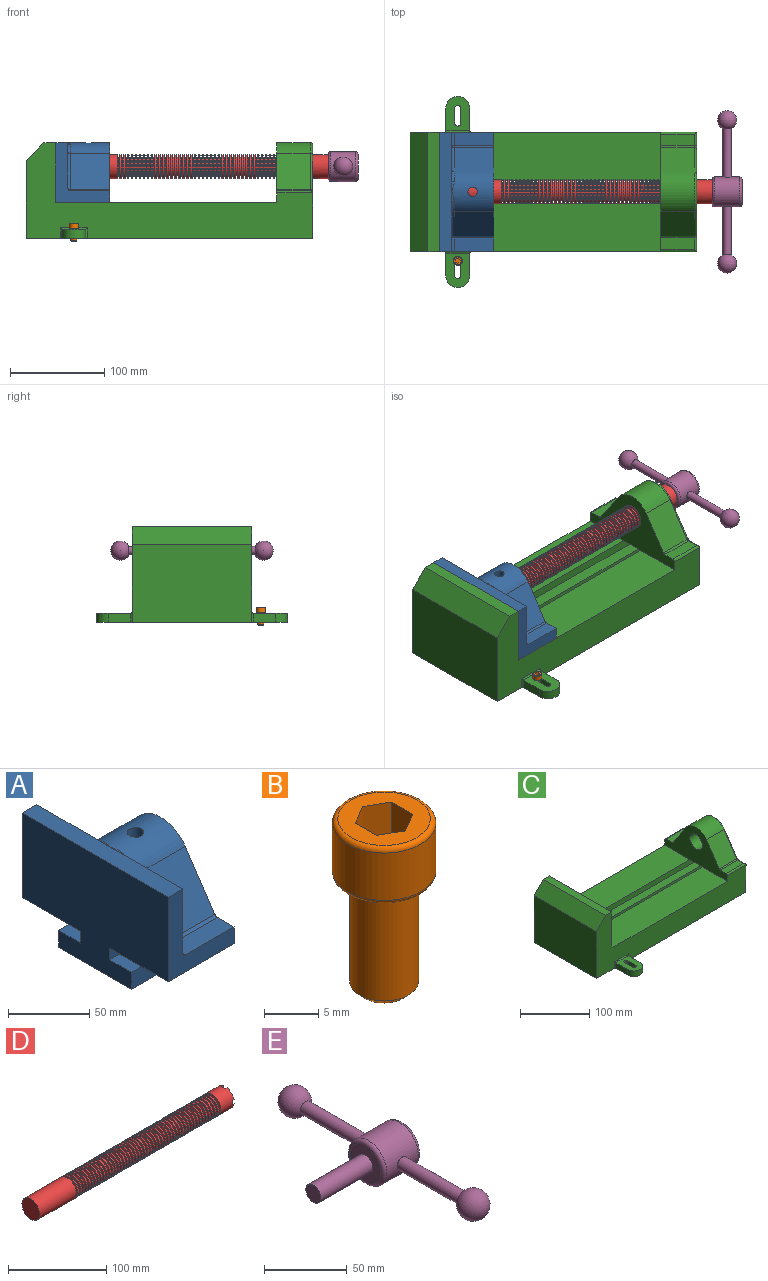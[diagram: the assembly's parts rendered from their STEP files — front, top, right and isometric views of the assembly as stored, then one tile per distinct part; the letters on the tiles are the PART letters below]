
ASSEMBLY  parts=5 mates=5
PART A: 36 faces, bbox 57.2x127x89 mm
  f0: plane 57.15x50.8mm, normal (0,0,-1), area 2903.2mm2, adj f6,f9,f10,f23
  f1: cylinder r=12.7mm len=44.45mm, axis (1,0,0), area 3464.3mm2, adj f6,f15,f16
  f2: plane 41.91x14.52mm, normal (0,0,1), area 608.5mm2, adj f6,f11,f24,f25
  f3: plane 51.86x48.26mm, normal (1,0,0), area 1495.7mm2, adj f8,f10,f31,f33,f35
  f4: plane 51.86x48.26mm, normal (1,0,0), area 1495.7mm2, adj f8,f11,f24,f28,f29
  f5: plane 57.15x50.8mm, normal (0,0,-1), area 2903.2mm2, adj f6,f9,f11,f22
  f6: plane 127x85.09mm, normal (1,0,0), area 5190.6mm2, adj f0,f1,f2,f5,f7,f10,f11,f12
  f7: plane 41.91x14.52mm, normal (0,0,1), area 608.5mm2, adj f6,f10,f30,f31
  f8: plane 127x12.7mm, normal (0,0,1), area 1612.9mm2, adj f3,f4,f9,f10,f11,f26,f34
  f9: plane 127x85.09mm, normal (-1,0,0), area 9096.8mm2, adj f0,f5,f8,f10,f11,f17,f18,f19
  f10: plane 63.5x57.15mm, normal (0,-1,0), area 1372.3mm2, adj f0,f3,f6,f7,f8,f9,f31
  f11: plane 63.5x57.15mm, normal (0,1,0), area 1372.3mm2, adj f2,f4,f5,f6,f8,f9,f24
  f12: plane 41.91x38.43mm, normal (0,-0.83,0.56), area 1939.2mm2, adj f6,f13,f30,f33
  f13: cylinder r=25.4mm len=44.45mm, axis (1,0,0), area 2026.5mm2, adj f6,f12,f14,f16,f26,f28,f34,f35
  f14: plane 41.91x38.43mm, normal (0,0.83,0.56), area 1939.2mm2, adj f6,f13,f25,f29
  f15: plane 25.4x25.4mm, normal (1,0,0), area 506.7mm2, adj f1
  f16: cylinder r=5.08mm len=13.76mm, axis (0,0,1), area 414mm2, adj f1,f13
  f17: plane 57.15x19.05mm, normal (0,0,1), area 1088.7mm2, adj f6,f9,f18,f23
  f18: plane 57.15x12.7mm, normal (0,-1,0), area 725.8mm2, adj f6,f9,f17,f19
  f19: plane 63.5x57.15mm, normal (0,0,-1), area 3629mm2, adj f6,f9,f18,f20
  f20: plane 57.15x12.7mm, normal (0,1,0), area 725.8mm2, adj f6,f9,f19,f21
  f21: plane 57.15x19.05mm, normal (0,0,1), area 1088.7mm2, adj f6,f9,f20,f22
  f22: plane 57.15x8.89mm, normal (0,1,0), area 508.1mm2, adj f5,f6,f9,f21
  f23: plane 57.15x8.89mm, normal (0,-1,0), area 508.1mm2, adj f0,f6,f9,f17
  f24: cylinder r=2.54mm len=14.52mm, axis (0,-1,0), area 57.9mm2, adj f2,f4,f11,f27
  f25: cylinder r=2.54mm len=41.91mm, axis (1,0,0), area 104.3mm2, adj f2,f6,f14,f27
  f26: bspline ~12.24x2.8mm, area 20.9mm2, adj f8,f13,f28
  f27: sphere r=2.54mm, area 6.3mm2, adj f24,f25,f29
  f28: torus R=27.94mm, axis (1,0,0), area 57.8mm2, adj f4,f13,f26,f29
  f29: cylinder r=2.54mm len=39.84mm, axis (0,-0.56,0.83), area 184.6mm2, adj f4,f14,f27,f28
  f30: cylinder r=2.54mm len=41.91mm, axis (1,0,0), area 104.3mm2, adj f6,f7,f12,f32
  f31: cylinder r=2.54mm len=14.52mm, axis (0,-1,0), area 57.9mm2, adj f3,f7,f10,f32
  f32: sphere r=2.54mm, area 6.3mm2, adj f30,f31,f33
  f33: cylinder r=2.54mm len=39.84mm, axis (0,-0.56,-0.83), area 184.6mm2, adj f3,f12,f32,f35
  f34: bspline ~12.24x2.8mm, area 20.9mm2, adj f8,f13,f35
  f35: torus R=27.94mm, axis (1,0,0), area 57.8mm2, adj f3,f13,f33,f34
PART B: 15 faces, bbox 10.3x10.3x19.1 mm
  f0: plane 8.51x8.51mm, normal (0,0,1), area 37.2mm2, adj f5,f6,f7,f8,f9,f10,f14
  f1: cylinder r=3.17mm len=11.94mm, axis (0,0,1), area 238.2mm2, adj f4,f12
  f2: plane 4.83x4.83mm, normal (0,0,-1), area 18.3mm2, adj f12
  f3: cylinder r=4.76mm len=9.53mm, axis (0,0,-1), area 159.6mm2, adj f13,f14
  f4: plane 8.51x8.51mm, normal (0,0,-1), area 25.2mm2, adj f1,f13
  f5: plane 4.83x2.38mm, normal (-0.5,-0.87,0), area 13.3mm2, adj f0,f6,f10,f11
  f6: plane 4.83x2.38mm, normal (0.5,-0.87,0), area 13.3mm2, adj f0,f5,f7,f11
  f7: plane 4.83x2.75mm, normal (1,0,0), area 13.3mm2, adj f0,f6,f8,f11
  f8: plane 4.83x2.38mm, normal (0.5,0.87,0), area 13.3mm2, adj f0,f7,f9,f11
  f9: plane 4.83x2.38mm, normal (-0.5,0.87,0), area 13.3mm2, adj f0,f8,f10,f11
  f10: plane 4.83x2.75mm, normal (-1,0,0), area 13.3mm2, adj f0,f5,f9,f11
  f11: plane 5.5x4.76mm, normal (0,0,1), area 19.6mm2, adj f5,f6,f7,f8,f9,f10
  f12: cone r=3.17mm half-angle=45deg, axis (0,0,1), area 18.9mm2, adj f1,f2
  f13: torus R=4.25mm, axis (0,0,1), area 23mm2, adj f3,f4
  f14: torus R=4.25mm, axis (0,0,1), area 23mm2, adj f0,f3
PART C: 61 faces, bbox 304.8x203.2x103.7 mm
  f0: plane 304.8x101.6mm, normal (0,1,0), area 13520.3mm2, adj f3,f4,f5,f6,f7,f8,f9,f16
  f1: plane 304.8x101.6mm, normal (0,-1,0), area 13520.3mm2, adj f2,f3,f5,f6,f7,f8,f9,f16
  f2: plane 234.95x50.8mm, normal (0,0,1), area 11935.5mm2, adj f1,f5,f16,f26
  f3: plane 127x99.06mm, normal (1,0,0), area 7097.5mm2, adj f0,f1,f9,f14,f17,f18,f19,f20
  f4: plane 234.95x50.8mm, normal (0,0,1), area 11935.5mm2, adj f0,f5,f16,f27
  f5: plane 127x101.6mm, normal (1,0,0), area 9516.1mm2, adj f0,f1,f2,f4,f6,f9,f18,f19
  f6: plane 127x12.7mm, normal (0,0,1), area 1612.9mm2, adj f0,f1,f5,f7
  f7: plane 127x19.05mm, normal (-0.71,0,0.71), area 3421.5mm2, adj f0,f1,f6,f8
  f8: plane 127x82.55mm, normal (-1,0,0), area 10483.8mm2, adj f0,f1,f7,f9
  f9: plane 304.8x203.2mm, normal (0,0,-1), area 33298.3mm2, adj f0,f1,f3,f5,f8,f21,f22,f39
  f10: plane 35.56x11.98mm, normal (0,0,1), area 426mm2, adj f16,f28,f29,f30
  f11: plane 38.43x35.56mm, normal (0,0.83,0.56), area 1645.4mm2, adj f12,f16,f29,f32
  f12: cylinder r=25.4mm len=42.19mm, axis (1,0,0), area 1770.2mm2, adj f11,f13,f16,f33
  f13: plane 38.43x35.56mm, normal (0,-0.83,0.56), area 1645.4mm2, adj f12,f16,f34,f35
  f14: cylinder r=12.7mm len=38.1mm, axis (1,0,0), area 3040.2mm2, adj f3,f16
  f15: plane 35.56x11.98mm, normal (0,0,1), area 426mm2, adj f16,f34,f36,f38
  f16: plane 127x63.5mm, normal (-1,0,0), area 4155.5mm2, adj f0,f1,f2,f4,f10,f11,f12,f13
  f17: plane 38.1x25.4mm, normal (0,0,-1), area 967.7mm2, adj f3,f16,f26,f27
  f18: plane 273.05x19.05mm, normal (0,0,-1), area 5201.6mm2, adj f3,f5,f19,f26
  f19: plane 273.05x12.7mm, normal (0,1,0), area 3467.7mm2, adj f3,f5,f18,f20
  f20: plane 273.05x19.05mm, normal (0,0,1), area 5201.6mm2, adj f3,f5,f19,f21
  f21: plane 273.05x16.51mm, normal (0,1,0), area 4508.1mm2, adj f3,f5,f9,f20
  f22: plane 273.05x16.51mm, normal (0,-1,0), area 4508.1mm2, adj f3,f5,f9,f23
  f23: plane 273.05x19.05mm, normal (0,0,1), area 5201.6mm2, adj f3,f5,f22,f24
  f24: plane 273.05x12.7mm, normal (0,-1,0), area 3467.7mm2, adj f3,f5,f23,f25
  f25: plane 273.05x19.05mm, normal (0,0,-1), area 5201.6mm2, adj f3,f5,f24,f27
  f26: plane 273.05x8.89mm, normal (0,1,0), area 2427.4mm2, adj f2,f3,f5,f17,f18
  f27: plane 273.05x8.89mm, normal (0,-1,0), area 2427.4mm2, adj f3,f4,f5,f17,f25
  f28: cylinder r=2.54mm len=38.1mm, axis (1,0,0), area 148.3mm2, adj f0,f10,f16,f30
  f29: cylinder r=2.54mm len=35.56mm, axis (-1,0,0), area 88.5mm2, adj f10,f11,f16,f31
  f30: cylinder r=2.54mm len=14.52mm, axis (0,1,0), area 54.3mm2, adj f3,f10,f28,f31
  f31: torus R=5.08mm, axis (-1,0,0), area 13.5mm2, adj f3,f29,f30,f32
  f32: cylinder r=2.54mm len=39.84mm, axis (0,0.56,-0.83), area 184.6mm2, adj f3,f11,f31,f33
  f33: torus R=22.86mm, axis (-1,0,0), area 191.4mm2, adj f3,f12,f32,f35
  f34: cylinder r=2.54mm len=35.56mm, axis (-1,0,0), area 88.5mm2, adj f13,f15,f16,f37
  f35: cylinder r=2.54mm len=39.84mm, axis (0,0.56,0.83), area 184.6mm2, adj f3,f13,f33,f37
  f36: cylinder r=2.54mm len=38.1mm, axis (-1,0,0), area 148.3mm2, adj f1,f15,f16,f38
  f37: torus R=5.08mm, axis (-1,0,0), area 13.5mm2, adj f3,f34,f35,f38
  f38: cylinder r=2.54mm len=14.52mm, axis (0,1,0), area 54.3mm2, adj f3,f15,f36,f37
  f39: plane 23.88x9.53mm, normal (-1,0,0), area 227.4mm2, adj f9,f45,f46,f60
  f40: plane 23.88x9.53mm, normal (1,0,0), area 227.4mm2, adj f9,f45,f46,f58
  f41: cylinder r=3.3mm len=9.53mm, axis (0,0,-1), area 98.8mm2, adj f9,f42,f44,f46
  f42: plane 15.62x9.53mm, normal (-1,0,0), area 148.8mm2, adj f9,f41,f43,f46
  f43: cylinder r=3.3mm len=9.53mm, axis (0,0,-1), area 98.8mm2, adj f9,f42,f44,f46
  f44: plane 15.62x9.53mm, normal (1,0,0), area 148.8mm2, adj f9,f41,f43,f46
  f45: cylinder r=12.7mm len=25.4mm, axis (0,0,-1), area 380mm2, adj f9,f39,f40,f46
  f46: plane 36.58x25.4mm, normal (0,0,1), area 722.4mm2, adj f39,f40,f41,f42,f43,f44,f45,f59
  f47: plane 23.88x9.53mm, normal (-1,0,0), area 227.4mm2, adj f9,f53,f54,f56
  f48: plane 23.88x9.53mm, normal (1,0,0), area 227.4mm2, adj f9,f53,f54,f55
  f49: cylinder r=3.3mm len=9.53mm, axis (0,0,-1), area 98.8mm2, adj f9,f50,f52,f54
  f50: plane 15.62x9.53mm, normal (-1,0,0), area 148.8mm2, adj f9,f49,f51,f54
  f51: cylinder r=3.3mm len=9.53mm, axis (0,0,-1), area 98.8mm2, adj f9,f50,f52,f54
  f52: plane 15.62x9.53mm, normal (1,0,0), area 148.8mm2, adj f9,f49,f51,f54
  f53: cylinder r=12.7mm len=25.4mm, axis (0,0,-1), area 380mm2, adj f9,f47,f48,f54
  f54: plane 36.58x25.4mm, normal (0,0,1), area 722.4mm2, adj f47,f48,f49,f50,f51,f52,f53,f57
  f55: cylinder r=1.52mm len=11.05mm, axis (0,0,-1), area 24.1mm2, adj f0,f9,f48,f57
  f56: cylinder r=1.52mm len=11.05mm, axis (0,0,1), area 24.1mm2, adj f0,f9,f47,f57
  f57: cylinder r=1.52mm len=28.45mm, axis (1,0,0), area 63.5mm2, adj f0,f54,f55,f56
  f58: cylinder r=1.52mm len=11.05mm, axis (0,0,1), area 24.1mm2, adj f1,f9,f40,f59
  f59: cylinder r=1.52mm len=28.45mm, axis (-1,0,0), area 63.5mm2, adj f1,f46,f58,f60
  f60: cylinder r=1.52mm len=11.05mm, axis (0,0,-1), area 24.1mm2, adj f1,f9,f39,f59
PART D: 220 faces, bbox 279.4x25.4x25.4 mm
  f0: cylinder r=12.7mm len=25.4mm, axis (-1,0,0), area 1468.2mm2, adj f1,f2,f3,f5,f7,f208,f209,f210
  f1: plane 9.9x9.9mm, normal (1,0,0), area 62.3mm2, adj f0,f4,f213,f216
  f2: plane 9.9x9.9mm, normal (1,0,0), area 62.3mm2, adj f0,f4,f210,f218
  f3: plane 9.9x9.9mm, normal (1,0,0), area 62.3mm2, adj f0,f4,f209,f212
  f4: cylinder r=6.35mm len=25.4mm, axis (1,0,0), area 960.3mm2, adj f1,f2,f3,f5,f6,f208,f209,f210
  f5: plane 9.9x9.9mm, normal (1,0,0), area 62.3mm2, adj f0,f4,f215,f217
  f6: plane 12.7x12.7mm, normal (1,0,0), area 126.7mm2, adj f4
  f7: cone r=12.7mm half-angle=76deg, axis (1,0,0), area 188mm2, adj f0,f9
  f8: cone r=10.16mm half-angle=76deg, axis (-1,0,0), area 188mm2, adj f9,f10
  f9: cylinder r=10.16mm len=20.32mm, axis (1,0,0), area 81.1mm2, adj f7,f8
  f10: cylinder r=12.7mm len=25.4mm, axis (-1,0,0), area 131.7mm2, adj f8,f11
  f11: cone r=12.7mm half-angle=76deg, axis (1,0,0), area 188mm2, adj f10,f13
  f12: cone r=10.16mm half-angle=76deg, axis (-1,0,0), area 188mm2, adj f13,f14
  f13: cylinder r=10.16mm len=20.32mm, axis (1,0,0), area 81.1mm2, adj f11,f12
  f14: cylinder r=12.7mm len=25.4mm, axis (-1,0,0), area 131.7mm2, adj f12,f15
  f15: cone r=12.7mm half-angle=76deg, axis (1,0,0), area 188mm2, adj f14,f17
  f16: cone r=10.16mm half-angle=76deg, axis (-1,0,0), area 188mm2, adj f17,f18
  f17: cylinder r=10.16mm len=20.32mm, axis (1,0,0), area 81.1mm2, adj f15,f16
  f18: cylinder r=12.7mm len=25.4mm, axis (-1,0,0), area 131.7mm2, adj f16,f19
  f19: cone r=12.7mm half-angle=76deg, axis (1,0,0), area 188mm2, adj f18,f21
  f20: cone r=10.16mm half-angle=76deg, axis (-1,0,0), area 188mm2, adj f21,f22
  f21: cylinder r=10.16mm len=20.32mm, axis (1,0,0), area 81.1mm2, adj f19,f20
  f22: cylinder r=12.7mm len=25.4mm, axis (-1,0,0), area 131.7mm2, adj f20,f23
  f23: cone r=12.7mm half-angle=76deg, axis (1,0,0), area 188mm2, adj f22,f25
  f24: cone r=10.16mm half-angle=76deg, axis (-1,0,0), area 188mm2, adj f25,f26
  f25: cylinder r=10.16mm len=20.32mm, axis (1,0,0), area 81.1mm2, adj f23,f24
  f26: cylinder r=12.7mm len=25.4mm, axis (-1,0,0), area 131.7mm2, adj f24,f27
  f27: cone r=12.7mm half-angle=76deg, axis (1,0,0), area 188mm2, adj f26,f29
  f28: cone r=10.16mm half-angle=76deg, axis (-1,0,0), area 188mm2, adj f29,f30
  f29: cylinder r=10.16mm len=20.32mm, axis (1,0,0), area 81.1mm2, adj f27,f28
  f30: cylinder r=12.7mm len=25.4mm, axis (-1,0,0), area 131.7mm2, adj f28,f31
  f31: cone r=12.7mm half-angle=76deg, axis (1,0,0), area 188mm2, adj f30,f33
  f32: cone r=10.16mm half-angle=76deg, axis (-1,0,0), area 188mm2, adj f33,f34
  f33: cylinder r=10.16mm len=20.32mm, axis (1,0,0), area 81.1mm2, adj f31,f32
  f34: cylinder r=12.7mm len=25.4mm, axis (-1,0,0), area 131.7mm2, adj f32,f35
  f35: cone r=12.7mm half-angle=76deg, axis (1,0,0), area 188mm2, adj f34,f37
  f36: cone r=10.16mm half-angle=76deg, axis (-1,0,0), area 188mm2, adj f37,f38
  f37: cylinder r=10.16mm len=20.32mm, axis (1,0,0), area 81.1mm2, adj f35,f36
  f38: cylinder r=12.7mm len=25.4mm, axis (-1,0,0), area 131.7mm2, adj f36,f39
  f39: cone r=12.7mm half-angle=76deg, axis (1,0,0), area 188mm2, adj f38,f41
  f40: cone r=10.16mm half-angle=76deg, axis (-1,0,0), area 188mm2, adj f41,f42
  f41: cylinder r=10.16mm len=20.32mm, axis (1,0,0), area 81.1mm2, adj f39,f40
  f42: cylinder r=12.7mm len=25.4mm, axis (-1,0,0), area 131.7mm2, adj f40,f43
  f43: cone r=12.7mm half-angle=76deg, axis (1,0,0), area 188mm2, adj f42,f45
  f44: cone r=10.16mm half-angle=76deg, axis (-1,0,0), area 188mm2, adj f45,f46
  f45: cylinder r=10.16mm len=20.32mm, axis (1,0,0), area 81.1mm2, adj f43,f44
  f46: cylinder r=12.7mm len=25.4mm, axis (-1,0,0), area 131.7mm2, adj f44,f47
  f47: cone r=12.7mm half-angle=76deg, axis (1,0,0), area 188mm2, adj f46,f49
  f48: cone r=10.16mm half-angle=76deg, axis (-1,0,0), area 188mm2, adj f49,f50
  f49: cylinder r=10.16mm len=20.32mm, axis (1,0,0), area 81.1mm2, adj f47,f48
  f50: cylinder r=12.7mm len=25.4mm, axis (-1,0,0), area 131.7mm2, adj f48,f51
  f51: cone r=12.7mm half-angle=76deg, axis (1,0,0), area 188mm2, adj f50,f53
  f52: cone r=10.16mm half-angle=76deg, axis (-1,0,0), area 188mm2, adj f53,f54
  f53: cylinder r=10.16mm len=20.32mm, axis (1,0,0), area 81.1mm2, adj f51,f52
  f54: cylinder r=12.7mm len=25.4mm, axis (-1,0,0), area 131.7mm2, adj f52,f55
  f55: cone r=12.7mm half-angle=76deg, axis (1,0,0), area 188mm2, adj f54,f57
  f56: cone r=10.16mm half-angle=76deg, axis (-1,0,0), area 188mm2, adj f57,f58
  f57: cylinder r=10.16mm len=20.32mm, axis (1,0,0), area 81.1mm2, adj f55,f56
  f58: cylinder r=12.7mm len=25.4mm, axis (-1,0,0), area 131.7mm2, adj f56,f59
  f59: cone r=12.7mm half-angle=76deg, axis (1,0,0), area 188mm2, adj f58,f61
  f60: cone r=10.16mm half-angle=76deg, axis (-1,0,0), area 188mm2, adj f61,f62
  f61: cylinder r=10.16mm len=20.32mm, axis (1,0,0), area 81.1mm2, adj f59,f60
  f62: cylinder r=12.7mm len=25.4mm, axis (-1,0,0), area 131.7mm2, adj f60,f63
  f63: cone r=12.7mm half-angle=76deg, axis (1,0,0), area 188mm2, adj f62,f65
  f64: cone r=10.16mm half-angle=76deg, axis (-1,0,0), area 188mm2, adj f65,f66
  f65: cylinder r=10.16mm len=20.32mm, axis (1,0,0), area 81.1mm2, adj f63,f64
  f66: cylinder r=12.7mm len=25.4mm, axis (-1,0,0), area 131.7mm2, adj f64,f67
  f67: cone r=12.7mm half-angle=76deg, axis (1,0,0), area 188mm2, adj f66,f69
  f68: cone r=10.16mm half-angle=76deg, axis (-1,0,0), area 188mm2, adj f69,f70
  f69: cylinder r=10.16mm len=20.32mm, axis (1,0,0), area 81.1mm2, adj f67,f68
  f70: cylinder r=12.7mm len=25.4mm, axis (-1,0,0), area 131.7mm2, adj f68,f71
  f71: cone r=12.7mm half-angle=76deg, axis (1,0,0), area 188mm2, adj f70,f73
  f72: cone r=10.16mm half-angle=76deg, axis (-1,0,0), area 188mm2, adj f73,f74
  f73: cylinder r=10.16mm len=20.32mm, axis (1,0,0), area 81.1mm2, adj f71,f72
  f74: cylinder r=12.7mm len=25.4mm, axis (-1,0,0), area 131.7mm2, adj f72,f75
  f75: cone r=12.7mm half-angle=76deg, axis (1,0,0), area 188mm2, adj f74,f77
  f76: cone r=10.16mm half-angle=76deg, axis (-1,0,0), area 188mm2, adj f77,f78
  f77: cylinder r=10.16mm len=20.32mm, axis (1,0,0), area 81.1mm2, adj f75,f76
  f78: cylinder r=12.7mm len=25.4mm, axis (-1,0,0), area 131.7mm2, adj f76,f79
  f79: cone r=12.7mm half-angle=76deg, axis (1,0,0), area 188mm2, adj f78,f81
  f80: cone r=10.16mm half-angle=76deg, axis (-1,0,0), area 188mm2, adj f81,f82
  f81: cylinder r=10.16mm len=20.32mm, axis (1,0,0), area 81.1mm2, adj f79,f80
  f82: cylinder r=12.7mm len=25.4mm, axis (-1,0,0), area 131.7mm2, adj f80,f83
  f83: cone r=12.7mm half-angle=76deg, axis (1,0,0), area 188mm2, adj f82,f85
  f84: cone r=10.16mm half-angle=76deg, axis (-1,0,0), area 188mm2, adj f85,f86
  f85: cylinder r=10.16mm len=20.32mm, axis (1,0,0), area 81.1mm2, adj f83,f84
  f86: cylinder r=12.7mm len=25.4mm, axis (-1,0,0), area 131.7mm2, adj f84,f87
  f87: cone r=12.7mm half-angle=76deg, axis (1,0,0), area 188mm2, adj f86,f89
  f88: cone r=10.16mm half-angle=76deg, axis (-1,0,0), area 188mm2, adj f89,f90
  f89: cylinder r=10.16mm len=20.32mm, axis (1,0,0), area 81.1mm2, adj f87,f88
  f90: cylinder r=12.7mm len=25.4mm, axis (-1,0,0), area 131.7mm2, adj f88,f91
  f91: cone r=12.7mm half-angle=76deg, axis (1,0,0), area 188mm2, adj f90,f93
  f92: cone r=10.16mm half-angle=76deg, axis (-1,0,0), area 188mm2, adj f93,f94
  f93: cylinder r=10.16mm len=20.32mm, axis (1,0,0), area 81.1mm2, adj f91,f92
  f94: cylinder r=12.7mm len=25.4mm, axis (-1,0,0), area 131.7mm2, adj f92,f95
  f95: cone r=12.7mm half-angle=76deg, axis (1,0,0), area 188mm2, adj f94,f97
  f96: cone r=10.16mm half-angle=76deg, axis (-1,0,0), area 188mm2, adj f97,f98
  f97: cylinder r=10.16mm len=20.32mm, axis (1,0,0), area 81.1mm2, adj f95,f96
  f98: cylinder r=12.7mm len=25.4mm, axis (-1,0,0), area 131.7mm2, adj f96,f99
  f99: cone r=12.7mm half-angle=76deg, axis (1,0,0), area 188mm2, adj f98,f101
  f100: cone r=10.16mm half-angle=76deg, axis (-1,0,0), area 188mm2, adj f101,f102
  f101: cylinder r=10.16mm len=20.32mm, axis (1,0,0), area 81.1mm2, adj f99,f100
  f102: cylinder r=12.7mm len=25.4mm, axis (-1,0,0), area 131.7mm2, adj f100,f103
  f103: cone r=12.7mm half-angle=76deg, axis (1,0,0), area 188mm2, adj f102,f105
  f104: cone r=10.16mm half-angle=76deg, axis (-1,0,0), area 188mm2, adj f105,f106
  f105: cylinder r=10.16mm len=20.32mm, axis (1,0,0), area 81.1mm2, adj f103,f104
  f106: cylinder r=12.7mm len=25.4mm, axis (-1,0,0), area 131.7mm2, adj f104,f107
  f107: cone r=12.7mm half-angle=76deg, axis (1,0,0), area 188mm2, adj f106,f109
  f108: cone r=10.16mm half-angle=76deg, axis (-1,0,0), area 188mm2, adj f109,f110
  f109: cylinder r=10.16mm len=20.32mm, axis (1,0,0), area 81.1mm2, adj f107,f108
  f110: cylinder r=12.7mm len=25.4mm, axis (-1,0,0), area 131.7mm2, adj f108,f111
  f111: cone r=12.7mm half-angle=76deg, axis (1,0,0), area 188mm2, adj f110,f113
  f112: cone r=10.16mm half-angle=76deg, axis (-1,0,0), area 188mm2, adj f113,f114
  f113: cylinder r=10.16mm len=20.32mm, axis (1,0,0), area 81.1mm2, adj f111,f112
  f114: cylinder r=12.7mm len=25.4mm, axis (-1,0,0), area 131.7mm2, adj f112,f115
  f115: cone r=12.7mm half-angle=76deg, axis (1,0,0), area 188mm2, adj f114,f117
  f116: cone r=10.16mm half-angle=76deg, axis (-1,0,0), area 188mm2, adj f117,f118
  f117: cylinder r=10.16mm len=20.32mm, axis (1,0,0), area 81.1mm2, adj f115,f116
  f118: cylinder r=12.7mm len=25.4mm, axis (-1,0,0), area 131.7mm2, adj f116,f119
  f119: cone r=12.7mm half-angle=76deg, axis (1,0,0), area 188mm2, adj f118,f121
  f120: cone r=10.16mm half-angle=76deg, axis (-1,0,0), area 188mm2, adj f121,f122
  f121: cylinder r=10.16mm len=20.32mm, axis (1,0,0), area 81.1mm2, adj f119,f120
  f122: cylinder r=12.7mm len=25.4mm, axis (-1,0,0), area 131.7mm2, adj f120,f123
  f123: cone r=12.7mm half-angle=76deg, axis (1,0,0), area 188mm2, adj f122,f125
  f124: cone r=10.16mm half-angle=76deg, axis (-1,0,0), area 188mm2, adj f125,f126
  f125: cylinder r=10.16mm len=20.32mm, axis (1,0,0), area 81.1mm2, adj f123,f124
  f126: cylinder r=12.7mm len=25.4mm, axis (-1,0,0), area 131.7mm2, adj f124,f127
  f127: cone r=12.7mm half-angle=76deg, axis (1,0,0), area 188mm2, adj f126,f129
  f128: cone r=10.16mm half-angle=76deg, axis (-1,0,0), area 188mm2, adj f129,f130
  f129: cylinder r=10.16mm len=20.32mm, axis (1,0,0), area 81.1mm2, adj f127,f128
  f130: cylinder r=12.7mm len=25.4mm, axis (-1,0,0), area 131.7mm2, adj f128,f131
  f131: cone r=12.7mm half-angle=76deg, axis (1,0,0), area 188mm2, adj f130,f133
  f132: cone r=10.16mm half-angle=76deg, axis (-1,0,0), area 188mm2, adj f133,f134
  f133: cylinder r=10.16mm len=20.32mm, axis (1,0,0), area 81.1mm2, adj f131,f132
  f134: cylinder r=12.7mm len=25.4mm, axis (-1,0,0), area 131.7mm2, adj f132,f135
  f135: cone r=12.7mm half-angle=76deg, axis (1,0,0), area 188mm2, adj f134,f137
  f136: cone r=10.16mm half-angle=76deg, axis (-1,0,0), area 188mm2, adj f137,f138
  f137: cylinder r=10.16mm len=20.32mm, axis (1,0,0), area 81.1mm2, adj f135,f136
  f138: cylinder r=12.7mm len=25.4mm, axis (-1,0,0), area 131.7mm2, adj f136,f139
  f139: cone r=12.7mm half-angle=76deg, axis (1,0,0), area 188mm2, adj f138,f141
  f140: cone r=10.16mm half-angle=76deg, axis (-1,0,0), area 188mm2, adj f141,f142
  f141: cylinder r=10.16mm len=20.32mm, axis (1,0,0), area 81.1mm2, adj f139,f140
  f142: cylinder r=12.7mm len=25.4mm, axis (-1,0,0), area 131.7mm2, adj f140,f143
  f143: cone r=12.7mm half-angle=76deg, axis (1,0,0), area 188mm2, adj f142,f145
  f144: cone r=10.16mm half-angle=76deg, axis (-1,0,0), area 188mm2, adj f145,f146
  f145: cylinder r=10.16mm len=20.32mm, axis (1,0,0), area 81.1mm2, adj f143,f144
  f146: cylinder r=12.7mm len=25.4mm, axis (-1,0,0), area 131.7mm2, adj f144,f147
  f147: cone r=12.7mm half-angle=76deg, axis (1,0,0), area 188mm2, adj f146,f149
  f148: cone r=10.16mm half-angle=76deg, axis (-1,0,0), area 188mm2, adj f149,f150
  f149: cylinder r=10.16mm len=20.32mm, axis (1,0,0), area 81.1mm2, adj f147,f148
  f150: cylinder r=12.7mm len=25.4mm, axis (-1,0,0), area 131.7mm2, adj f148,f151
  f151: cone r=12.7mm half-angle=76deg, axis (1,0,0), area 188mm2, adj f150,f153
  f152: cone r=10.16mm half-angle=76deg, axis (-1,0,0), area 188mm2, adj f153,f154
  f153: cylinder r=10.16mm len=20.32mm, axis (1,0,0), area 81.1mm2, adj f151,f152
  f154: cylinder r=12.7mm len=25.4mm, axis (-1,0,0), area 131.7mm2, adj f152,f155
  f155: cone r=12.7mm half-angle=76deg, axis (1,0,0), area 188mm2, adj f154,f157
  f156: cone r=10.16mm half-angle=76deg, axis (-1,0,0), area 188mm2, adj f157,f158
  f157: cylinder r=10.16mm len=20.32mm, axis (1,0,0), area 81.1mm2, adj f155,f156
  f158: cylinder r=12.7mm len=25.4mm, axis (-1,0,0), area 131.7mm2, adj f156,f159
  f159: cone r=12.7mm half-angle=76deg, axis (1,0,0), area 188mm2, adj f158,f161
  f160: cone r=10.16mm half-angle=76deg, axis (-1,0,0), area 188mm2, adj f161,f162
  f161: cylinder r=10.16mm len=20.32mm, axis (1,0,0), area 81.1mm2, adj f159,f160
  f162: cylinder r=12.7mm len=25.4mm, axis (-1,0,0), area 131.7mm2, adj f160,f163
  f163: cone r=12.7mm half-angle=76deg, axis (1,0,0), area 188mm2, adj f162,f165
  f164: cone r=10.16mm half-angle=76deg, axis (-1,0,0), area 188mm2, adj f165,f166
  f165: cylinder r=10.16mm len=20.32mm, axis (1,0,0), area 81.1mm2, adj f163,f164
  f166: cylinder r=12.7mm len=25.4mm, axis (-1,0,0), area 131.7mm2, adj f164,f167
  f167: cone r=12.7mm half-angle=76deg, axis (1,0,0), area 188mm2, adj f166,f169
  f168: cone r=10.16mm half-angle=76deg, axis (-1,0,0), area 188mm2, adj f169,f170
  f169: cylinder r=10.16mm len=20.32mm, axis (1,0,0), area 81.1mm2, adj f167,f168
  f170: cylinder r=12.7mm len=25.4mm, axis (-1,0,0), area 131.7mm2, adj f168,f171
  f171: cone r=12.7mm half-angle=76deg, axis (1,0,0), area 188mm2, adj f170,f173
  f172: cone r=10.16mm half-angle=76deg, axis (-1,0,0), area 188mm2, adj f173,f174
  f173: cylinder r=10.16mm len=20.32mm, axis (1,0,0), area 81.1mm2, adj f171,f172
  f174: cylinder r=12.7mm len=25.4mm, axis (-1,0,0), area 131.7mm2, adj f172,f175
  f175: cone r=12.7mm half-angle=76deg, axis (1,0,0), area 188mm2, adj f174,f177
  f176: cone r=10.16mm half-angle=76deg, axis (-1,0,0), area 188mm2, adj f177,f178
  f177: cylinder r=10.16mm len=20.32mm, axis (1,0,0), area 81.1mm2, adj f175,f176
  f178: cylinder r=12.7mm len=25.4mm, axis (-1,0,0), area 131.7mm2, adj f176,f179
  f179: cone r=12.7mm half-angle=76deg, axis (1,0,0), area 188mm2, adj f178,f181
  f180: cone r=10.16mm half-angle=76deg, axis (-1,0,0), area 188mm2, adj f181,f182
  f181: cylinder r=10.16mm len=20.32mm, axis (1,0,0), area 81.1mm2, adj f179,f180
  f182: cylinder r=12.7mm len=25.4mm, axis (-1,0,0), area 131.7mm2, adj f180,f183
  f183: cone r=12.7mm half-angle=76deg, axis (1,0,0), area 188mm2, adj f182,f185
  f184: cone r=10.16mm half-angle=76deg, axis (-1,0,0), area 188mm2, adj f185,f186
  f185: cylinder r=10.16mm len=20.32mm, axis (1,0,0), area 81.1mm2, adj f183,f184
  f186: cylinder r=12.7mm len=25.4mm, axis (-1,0,0), area 131.7mm2, adj f184,f187
  f187: cone r=12.7mm half-angle=76deg, axis (1,0,0), area 188mm2, adj f186,f189
  f188: cone r=10.16mm half-angle=76deg, axis (-1,0,0), area 188mm2, adj f189,f190
  f189: cylinder r=10.16mm len=20.32mm, axis (1,0,0), area 81.1mm2, adj f187,f188
  f190: cylinder r=12.7mm len=25.4mm, axis (-1,0,0), area 131.7mm2, adj f188,f191
  f191: cone r=12.7mm half-angle=76deg, axis (1,0,0), area 188mm2, adj f190,f193
  f192: cone r=10.16mm half-angle=76deg, axis (-1,0,0), area 188mm2, adj f193,f194
  f193: cylinder r=10.16mm len=20.32mm, axis (1,0,0), area 81.1mm2, adj f191,f192
  f194: cylinder r=12.7mm len=25.4mm, axis (-1,0,0), area 131.7mm2, adj f192,f195
  f195: cone r=12.7mm half-angle=76deg, axis (1,0,0), area 188mm2, adj f194,f197
  f196: cone r=10.16mm half-angle=76deg, axis (-1,0,0), area 188mm2, adj f197,f198
  f197: cylinder r=10.16mm len=20.32mm, axis (1,0,0), area 81.1mm2, adj f195,f196
  f198: cylinder r=12.7mm len=25.4mm, axis (-1,0,0), area 131.7mm2, adj f196,f199
  f199: cone r=12.7mm half-angle=76deg, axis (1,0,0), area 188mm2, adj f198,f201
  f200: cone r=10.16mm half-angle=76deg, axis (-1,0,0), area 188mm2, adj f201,f202
  f201: cylinder r=10.16mm len=20.32mm, axis (1,0,0), area 81.1mm2, adj f199,f200
  f202: cylinder r=12.7mm len=25.4mm, axis (-1,0,0), area 131.7mm2, adj f200,f203
  f203: cone r=12.7mm half-angle=76deg, axis (1,0,0), area 188mm2, adj f202,f205
  f204: cone r=10.16mm half-angle=76deg, axis (-1,0,0), area 188mm2, adj f205,f207
  f205: cylinder r=10.16mm len=20.32mm, axis (1,0,0), area 81.1mm2, adj f203,f204
  f206: plane 25.4x25.4mm, normal (-1,0,0), area 506.7mm2, adj f207
  f207: cylinder r=12.7mm len=52.45mm, axis (-1,0,0), area 4185.4mm2, adj f204,f206
  f208: plane 6.88x5.08mm, normal (1,0,0), area 32.7mm2, adj f0,f4,f209,f210
  f209: plane 6.62x2.54mm, normal (0,-1,0), area 16.8mm2, adj f0,f3,f4,f208
  f210: plane 6.62x2.54mm, normal (0,1,0), area 16.8mm2, adj f0,f2,f4,f208
  f211: plane 6.88x5.08mm, normal (1,0,0), area 32.7mm2, adj f0,f4,f212,f213
  f212: plane 6.62x2.54mm, normal (0,0,1), area 16.8mm2, adj f0,f3,f4,f211
  f213: plane 6.62x2.54mm, normal (0,0,-1), area 16.8mm2, adj f0,f1,f4,f211
  f214: plane 6.88x5.08mm, normal (1,0,0), area 32.7mm2, adj f0,f4,f215,f216
  f215: plane 6.62x2.54mm, normal (0,1,0), area 16.8mm2, adj f0,f4,f5,f214
  f216: plane 6.62x2.54mm, normal (0,-1,0), area 16.8mm2, adj f0,f1,f4,f214
  f217: plane 6.62x2.54mm, normal (0,0,-1), area 16.8mm2, adj f0,f4,f5,f219
  f218: plane 6.62x2.54mm, normal (0,0,1), area 16.8mm2, adj f0,f2,f4,f219
  f219: plane 6.88x5.08mm, normal (1,0,0), area 32.7mm2, adj f0,f4,f217,f218
PART E: 11 faces, bbox 76.2x172.7x34.4 mm
  f0: sphere r=10.16mm, area 1231.8mm2, adj f1
  f1: cylinder r=4.45mm len=51.82mm, axis (0,1,0), area 1438.5mm2, adj f0,f4
  f2: sphere r=10.16mm, area 1231.8mm2, adj f3
  f3: cylinder r=4.45mm len=51.82mm, axis (0,1,0), area 1438.5mm2, adj f2,f4
  f4: cylinder r=15.88mm len=31.75mm, axis (-1,0,0), area 2534.7mm2, adj f1,f3,f9,f10
  f5: cylinder r=6.35mm len=44.45mm, axis (-1,0,0), area 1773.5mm2, adj f6,f8
  f6: plane 12.7x12.7mm, normal (-1,0,0), area 126.7mm2, adj f5
  f7: plane 26.67x26.67mm, normal (1,0,0), area 558.6mm2, adj f10
  f8: plane 26.67x26.67mm, normal (-1,0,0), area 432mm2, adj f5,f9
  f9: torus R=13.33mm, axis (1,0,0), area 374.8mm2, adj f4,f8
  f10: torus R=13.33mm, axis (1,0,0), area 374.8mm2, adj f4,f7
PLACE A at identity
PLACE B rot(axis=(0,0,1),61.4deg) t=(-254,-73.28,9.52)mm
PLACE C at identity fixed
PLACE D rot(axis=(-1,0,0),180deg) t=(0,0,152.4)mm
PLACE E rot(axis=(-1,0,0),180deg) t=(-21.59,0,152.4)mm
MATE fastened D.f4 <-> E.f5  axis (1,0,0) through (16.51,0,76.2)mm
MATE planar A.f0 <-> C.f2  axis (0,0,-1) through (-244.48,-38.1,38.1)mm
MATE pin_slot B.f1 <-> C.f41  axis (0,0,1) through (-254,-73.28,9.52)mm
MATE revolute D.f7 <-> A.f28  axis (-1,0,0) through (-260.35,0,76.2)mm
MATE cylindrical C.f12 <-> D.f7  axis (-1,0,0) through (-38.1,0,76.2)mm
